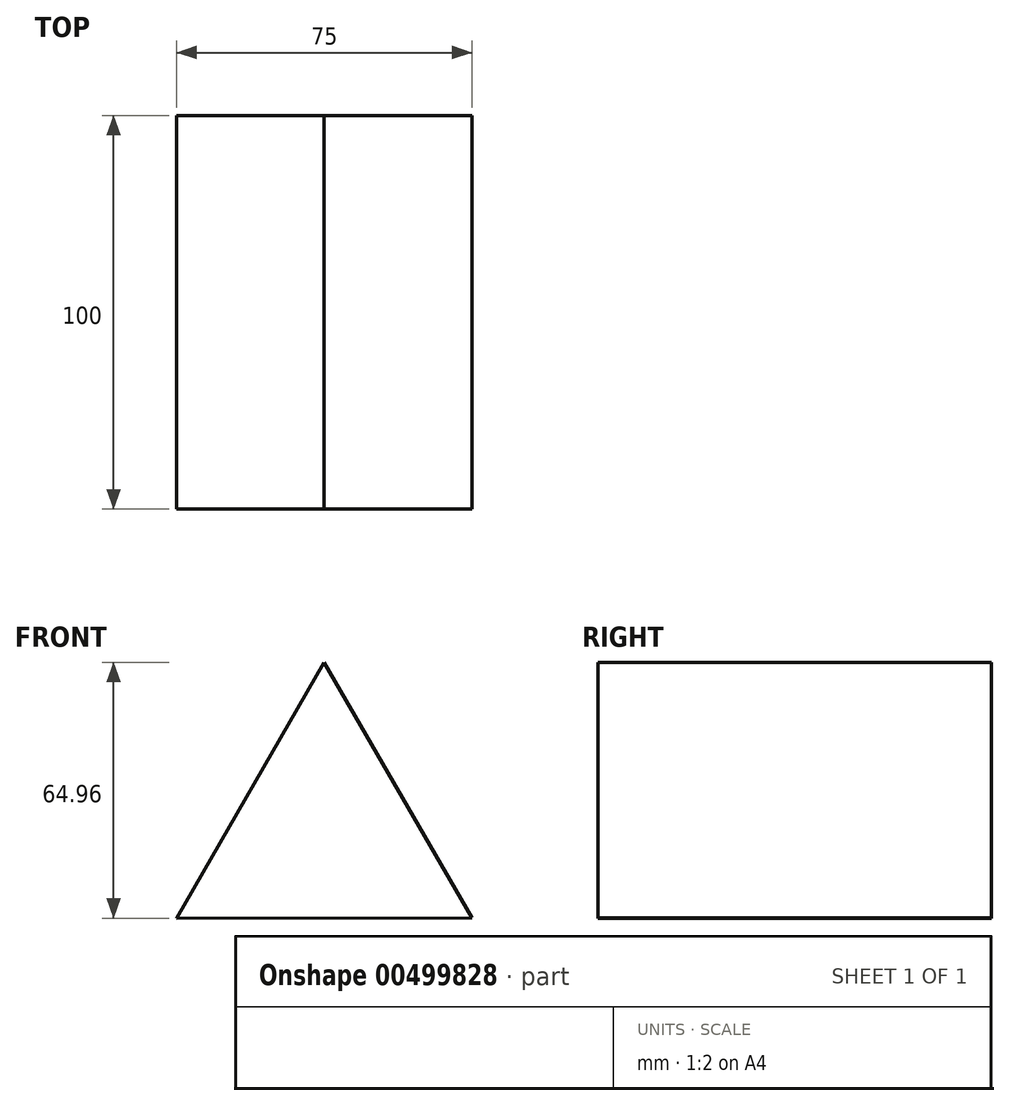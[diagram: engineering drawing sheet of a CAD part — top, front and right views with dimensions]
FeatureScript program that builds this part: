
annotation { "Feature Type Name" : "Feature", "Feature Type Description" : "" }
export const myFeature = defineFeature(function(context is Context, id is Id, definition is map)
    precondition{}
    {
        {
            var Q0;
            Q0=qCreatedBy(makeId("Front.planeOp"),FACE);
            var sketch = newSketch(context, id + "F0", { "sketchPlane" : qUnion([Q0])});
            skCircle(sketch, "E0.cCircle", {"center": v(0, 0) * mm, "radius": 21.65 * mm, "construction": true});
            skLineSegment(sketch, "E0.0", {"start": v(-0.01, 43.3) * mm, "end": v(37.5, -21.64) * mm});
            skLineSegment(sketch, "E0.1", {"start": v(37.5, -21.64) * mm, "end": v(-37.5, -21.66) * mm});
            skLineSegment(sketch, "E0.2", {"start": v(-37.5, -21.66) * mm, "end": v(-0.01, 43.3) * mm});
            skPoint(sketch, "E0.0.midPoint", {"position": v(18.75, 10.83) * mm});
            skSolve(sketch);
        }
        {
            var Q0;
            Q0 = qSketchRegion(id + "F0", true);
            extrude(context, id + "F1", {"entities" : qUnion([Q0]), "depth" : 100 * mm, "symmetric" : true});
        }
    });
